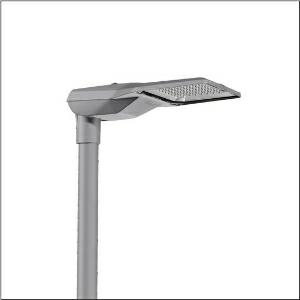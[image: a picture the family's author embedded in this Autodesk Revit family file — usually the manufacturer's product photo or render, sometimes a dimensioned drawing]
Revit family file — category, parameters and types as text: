
# Revit family: streetlight_sl_21_midi___st1_5a_5xe3p33s08mb_c1a7
name_source: partatom
category: Lighting Fixtures
units: mm (PartAtom-declared; Revit-internal decimal feet)

## family parameters
Cut with Voids When Loaded = No
Host = Face
Light Source = No
Part Type = Normal
Room Calculation Point = No
Round Connector Dimension = Use Diameter
Shared = No

## types (1)
- --- (1 x LED, 17960 lm, 136 W, 3000K)
    Apparent Load = 136 VA
    CIE Flux Codes = 22 53 95 100 100
    Color Rendering = 70
    Color Temperature = 3000K
    Default Elevation = 1800 mm
    Description = Streetlight SL 21 midi, mast luminaire, primary light control with lens, of PMMA, primary optical cover: cover, of toughened safety glass, transparent, light distribution: ST1.5a, light emission: direct distribution, primary light characteristic: asymmetric, installation type: side-entry, post-top, LED, High Power LED, rated luminous flux: 17.960lm, luminous efficacy: 132lm/W, light colour: 730, colour temperature: 3000K, control gear: D4i, control: overheat protection, constant luminous flux control, time-dependent luminous flux control, flexible luminous flux parameterisation, pre-setting: logarithmic dimming characteristic, mains connection: 230..240V, AC, 50/60Hz, start of lifetime: 136W, end of service life: 142W, reduction: 61W, luminaire housing, of diecast aluminium, powder-coated, Siteco® metallic grey (DB 702S), corrosivity category C5 mid according to DIN EN ISO 12944, please order mast flange separately, inclination adjustable: 0°, 5°, 10°, 15°, sealing non-destructively replaceable, multi-level sealing system, length: 644mm, width: 335mm, height: 110mm, mast flange for spigot size: 42mm (side-entry): 5XC10008XM4, 60/48mm (side-entry/post-top): 5XC10108XM2, 76/60mm (side-entry/post-top): 5XC10108XM1, mounting height: 4..8m, Smart Interface above, protection rating (complete): IP66, insulation class (complete): insulation class II (safety insulation), certification: CE, ENEC, ENEC+, VDE, impact resistance: IK10, permissible operating ambient temperature for outdoor applications: -40..+50°C, standard-compliant lighting for roads and squares, packaging unit: 1 piece

Light Distribution: ST1.5a
    Height = 111 mm
    Lamp = 1 x LED
    Lamp Light Flux = 17960 lm
    Lamp Power = 136 W
    Lamp count = 1
    Length = 644 mm
    Luminous efficacy = 132 lm/W
    Manufacturer = Siteco
    ModVariant = No
    Model = 5XE3P33S08MB
    Number of Poles = 1
    OnlyDefault = Yes
    Power Factor = 1
    Product Name = Streetlight SL 21 midi | ST1.5a
    Product group = mast luminaire | pylon top
    ProductGroupID = 6100
    Protection Class = Protection class II
    Protection Degree = IP 66
    RLX_Detail_Level = 1
    RLX_Emergency_Light_Flux = 0 lm
    RLX_Emergency_Type = 0
    RLX_Emergency_Type_DB = No
    RlxData = <blob elided: 30377 chars, md5=bea20c94>
    Socket = socket
    Standby Power = 0 W
    System Light Flux = 17960 lm
    System Power = 136 W
    Type Comments = factory setting: luminous flux: 100 % | dim-lin: 254 | 695 mA
    Type Image = l_1004302.jpg
    URL = http://relux.com
    VarID = @adj_197647
    Voltage = 0 V
    Weight = 0.00 kg
    Width = 336 mm

## geometry (parser evidence)
native form markers: Blend x4, Sweep x12
no freeform markers — native parametric forms only
